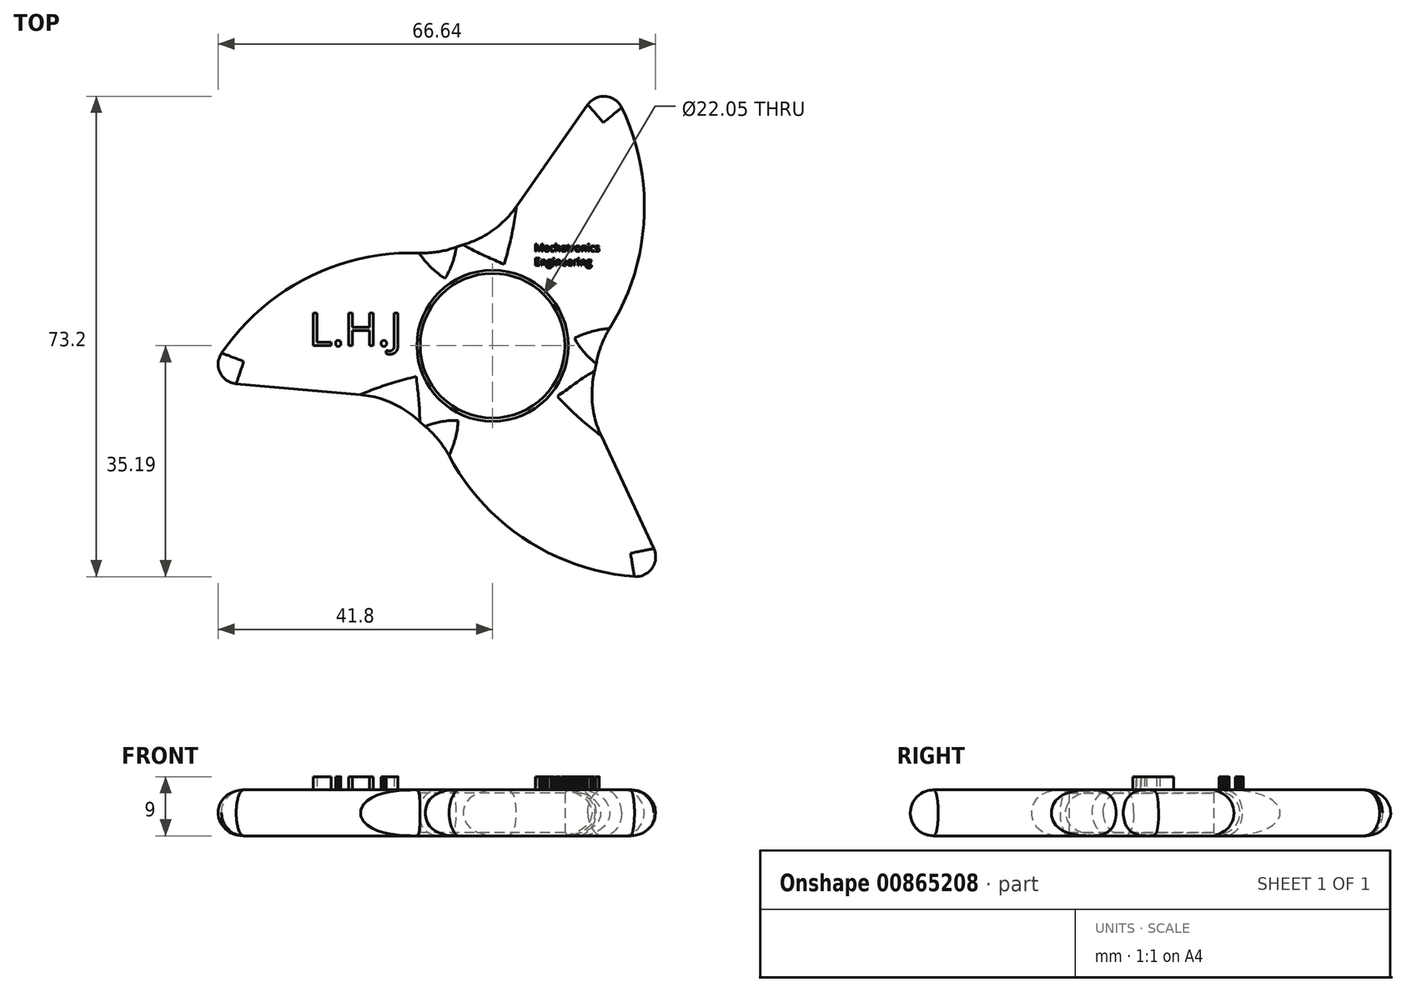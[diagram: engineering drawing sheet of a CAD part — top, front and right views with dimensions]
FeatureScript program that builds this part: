
annotation { "Feature Type Name" : "Feature", "Feature Type Description" : "" }
export const myFeature = defineFeature(function(context is Context, id is Id, definition is map)
    precondition{}
    {
        {
            var Q0;
            Q0=qCreatedBy(makeId("Top.planeOp"),FACE);
            var sketch = newSketch(context, id + "F0", { "sketchPlane" : qUnion([Q0])});
            skCircle(sketch, "E0", {"center": v(0, 0) * mm, "radius": 11.03 * mm});
            skCircle(sketch, "E1", {"center": v(0, 0) * mm, "radius": 16.03 * mm});
            skLineSegment(sketch, "E2", {"start": v(0, 16.02) * mm, "end": v(14.5, 36.73) * mm});
            skArc(sketch, "E3", {"start": v(16.03, 0) * mm, "mid": v(22.95, 17.64) * mm, "end": v(19.66, 36.31) * mm});
            skPoint(sketch, "E4.visualSharp", {"position": v(17.2, 40.6) * mm});
            skArc(sketch, "E4.filletArc", {"start": v(19.66, 36.31) * mm, "mid": v(17.2, 38) * mm, "end": v(14.5, 36.73) * mm});
            skSolve(sketch);
        }
        {
            var Q0;
            Q0=qSketchRegion(id+"F0",true);
            extrude(context, id + "F1", {"entities" : qUnion([Q0]), "depth" : 7 * mm, "offsetDistance" : 25 * mm});
        }
        {
            var Q0;
            Q0=qCreatedBy(makeId("Right.planeOp"),FACE);
            var sketch = newSketch(context, id + "F2", { "sketchPlane" : qUnion([Q0])});
            skLineSegment(sketch, "E5", {"start": v(0, 0) * mm, "end": v(0, -17.5) * mm});
            skSolve(sketch);
        }
        {
            var Q0;
            Q0=makeQuery(id+"F1.opExtrude","CAP_EDGE",EDGE,{"disambiguationData":[OSD([sQuery(id+"F0.wireOp",EDGE,"E3")])],"isStart":false});
            var Q1;
            Q1=makeQuery(id+"F1.opExtrude","CAP_EDGE",EDGE,{"disambiguationData":[OSD([sQuery(id+"F0.wireOp",EDGE,"E3")])],"isStart":true});
            var Q2;
            Q2=makeQuery(id+"F1.opExtrude","CAP_EDGE",EDGE,{"disambiguationData":[OSD([sQuery(id+"F0.wireOp",EDGE,"E1")])],"isStart":true});
            var Q3;
            Q3=makeQuery(id+"F1.opExtrude","CAP_EDGE",EDGE,{"disambiguationData":[OSD([sQuery(id+"F0.wireOp",EDGE,"E1")])],"isStart":false});
            fillet(context, id + "F3", {"entities" : qUnion([Q0, Q1, Q2, Q3]), "radius" : 3.5 * mm, "tangentPropagation" : true, "allowEdgeOverflow" : false});
        }
        {
            var Q0;
            Q0=makeQuery(id+"F1.opExtrude","SWEPT_BODY",BODY,{"disambiguationData":[OSD([sQuery(id+"F0.wireOp",EDGE,"E0"),sQuery(id+"F0.wireOp",EDGE,"E1"),sQuery(id+"F0.wireOp",EDGE,"E2"),sQuery(id+"F0.wireOp",EDGE,"E3"),sQuery(id+"F0.wireOp",EDGE,"E4.filletArc")])]});
            var Q1;
            Q1=sQuery(id+"F2.wireOp",EDGE,"E5");
            circularPattern(context, id + "F4", {"entities" : qUnion([Q0]), "axis" : qUnion([Q1]), "angle" : 360 * degree, "instanceCount" : 3, "equalSpace" : true});
        }
        {
            var Q0;
            Q0=makeQuery(id+"F1.opExtrude","SWEPT_BODY",BODY,{"disambiguationData":[OSD([sQuery(id+"F0.wireOp",EDGE,"E0"),sQuery(id+"F0.wireOp",EDGE,"E1"),sQuery(id+"F0.wireOp",EDGE,"E2"),sQuery(id+"F0.wireOp",EDGE,"E3"),sQuery(id+"F0.wireOp",EDGE,"E4.filletArc")])]});
            var Q1;
            Q1=makeQuery(id+"F4.opPattern","COPY",BODY,{"derivedFrom":makeQuery(id+"F1.opExtrude","SWEPT_BODY",BODY,{"disambiguationData":[OSD([sQuery(id+"F0.wireOp",EDGE,"E0"),sQuery(id+"F0.wireOp",EDGE,"E1"),sQuery(id+"F0.wireOp",EDGE,"E2"),sQuery(id+"F0.wireOp",EDGE,"E3"),sQuery(id+"F0.wireOp",EDGE,"E4.filletArc")])]}),"instanceName":"1"});
            var Q2;
            Q2=makeQuery(id+"F4.opPattern","COPY",BODY,{"derivedFrom":makeQuery(id+"F1.opExtrude","SWEPT_BODY",BODY,{"disambiguationData":[OSD([sQuery(id+"F0.wireOp",EDGE,"E0"),sQuery(id+"F0.wireOp",EDGE,"E1"),sQuery(id+"F0.wireOp",EDGE,"E2"),sQuery(id+"F0.wireOp",EDGE,"E3"),sQuery(id+"F0.wireOp",EDGE,"E4.filletArc")])]}),"instanceName":"2"});
            booleanBodies(context, id + "F5", {"operationType" : BooleanOperationType.UNION, "tools" : qUnion([Q0, Q1, Q2])});
        }
        {
            var Q0;
            {var subQ0=sQuery(id+"F0.wireOp",EDGE,"E2");var subQ1=sQuery(id+"F0.wireOp",EDGE,"E1");Q0=makeQuery(id+"F5.opBoolean","MERGE",EDGE,{"derivedFrom":[makeQuery(id+"F3.opFillet","BLEND_EDGE",EDGE,{"blendedFrom":[makeQuery(id+"F1.opExtrude","CAP_EDGE",EDGE,{"disambiguationData":[OSD([subQ1])],"isStart":true}),makeQuery(id+"F1.opExtrude","CAP_EDGE",EDGE,{"disambiguationData":[OSD([subQ0])],"isStart":true})],"blendedInto":[]}),makeQuery(id+"F3.opFillet","BLEND_EDGE",EDGE,{"blendedFrom":[makeQuery(id+"F1.opExtrude","CAP_EDGE",EDGE,{"disambiguationData":[OSD([subQ1])],"isStart":false}),makeQuery(id+"F1.opExtrude","CAP_EDGE",EDGE,{"disambiguationData":[OSD([subQ0])],"isStart":false})],"blendedInto":[]})]});}
            var Q1;
            {var subQ0=sQuery(id+"F0.wireOp",EDGE,"E3");var subQ1=sQuery(id+"F0.wireOp",EDGE,"E1");Q1=makeQuery(id+"F5.opBoolean","MERGE",EDGE,{"derivedFrom":[makeQuery(id+"F4.opPattern","COPY",EDGE,{"derivedFrom":makeQuery(id+"F3.opFillet","BLEND_EDGE",EDGE,{"blendedFrom":[makeQuery(id+"F1.opExtrude","CAP_EDGE",EDGE,{"disambiguationData":[OSD([subQ1])],"isStart":true}),makeQuery(id+"F1.opExtrude","CAP_EDGE",EDGE,{"disambiguationData":[OSD([subQ0])],"isStart":true})],"blendedInto":[]}),"instanceName":"2"}),makeQuery(id+"F4.opPattern","COPY",EDGE,{"derivedFrom":makeQuery(id+"F3.opFillet","BLEND_EDGE",EDGE,{"blendedFrom":[makeQuery(id+"F1.opExtrude","CAP_EDGE",EDGE,{"disambiguationData":[OSD([subQ1])],"isStart":false}),makeQuery(id+"F1.opExtrude","CAP_EDGE",EDGE,{"disambiguationData":[OSD([subQ0])],"isStart":false})],"blendedInto":[]}),"instanceName":"2"})]});}
            var Q2;
            {var subQ0=sQuery(id+"F0.wireOp",EDGE,"E3");var subQ1=sQuery(id+"F0.wireOp",EDGE,"E1");Q2=makeQuery(id+"F5.opBoolean","MERGE",EDGE,{"derivedFrom":[makeQuery(id+"F3.opFillet","BLEND_EDGE",EDGE,{"blendedFrom":[makeQuery(id+"F1.opExtrude","CAP_EDGE",EDGE,{"disambiguationData":[OSD([subQ1])],"isStart":true}),makeQuery(id+"F1.opExtrude","CAP_EDGE",EDGE,{"disambiguationData":[OSD([subQ0])],"isStart":true})],"blendedInto":[]}),makeQuery(id+"F3.opFillet","BLEND_EDGE",EDGE,{"blendedFrom":[makeQuery(id+"F1.opExtrude","CAP_EDGE",EDGE,{"disambiguationData":[OSD([subQ1])],"isStart":false}),makeQuery(id+"F1.opExtrude","CAP_EDGE",EDGE,{"disambiguationData":[OSD([subQ0])],"isStart":false})],"blendedInto":[]})]});}
            var Q3;
            {var subQ0=sQuery(id+"F0.wireOp",EDGE,"E2");var subQ1=sQuery(id+"F0.wireOp",EDGE,"E1");Q3=makeQuery(id+"F5.opBoolean","MERGE",EDGE,{"derivedFrom":[makeQuery(id+"F4.opPattern","COPY",EDGE,{"derivedFrom":makeQuery(id+"F3.opFillet","BLEND_EDGE",EDGE,{"blendedFrom":[makeQuery(id+"F1.opExtrude","CAP_EDGE",EDGE,{"disambiguationData":[OSD([subQ1])],"isStart":true}),makeQuery(id+"F1.opExtrude","CAP_EDGE",EDGE,{"disambiguationData":[OSD([subQ0])],"isStart":true})],"blendedInto":[]}),"instanceName":"1"}),makeQuery(id+"F4.opPattern","COPY",EDGE,{"derivedFrom":makeQuery(id+"F3.opFillet","BLEND_EDGE",EDGE,{"blendedFrom":[makeQuery(id+"F1.opExtrude","CAP_EDGE",EDGE,{"disambiguationData":[OSD([subQ1])],"isStart":false}),makeQuery(id+"F1.opExtrude","CAP_EDGE",EDGE,{"disambiguationData":[OSD([subQ0])],"isStart":false})],"blendedInto":[]}),"instanceName":"1"})]});}
            var Q4;
            {var subQ0=sQuery(id+"F0.wireOp",EDGE,"E3");var subQ1=sQuery(id+"F0.wireOp",EDGE,"E1");Q4=makeQuery(id+"F5.opBoolean","MERGE",EDGE,{"derivedFrom":[makeQuery(id+"F4.opPattern","COPY",EDGE,{"derivedFrom":makeQuery(id+"F3.opFillet","BLEND_EDGE",EDGE,{"blendedFrom":[makeQuery(id+"F1.opExtrude","CAP_EDGE",EDGE,{"disambiguationData":[OSD([subQ1])],"isStart":true}),makeQuery(id+"F1.opExtrude","CAP_EDGE",EDGE,{"disambiguationData":[OSD([subQ0])],"isStart":true})],"blendedInto":[]}),"instanceName":"1"}),makeQuery(id+"F4.opPattern","COPY",EDGE,{"derivedFrom":makeQuery(id+"F3.opFillet","BLEND_EDGE",EDGE,{"blendedFrom":[makeQuery(id+"F1.opExtrude","CAP_EDGE",EDGE,{"disambiguationData":[OSD([subQ1])],"isStart":false}),makeQuery(id+"F1.opExtrude","CAP_EDGE",EDGE,{"disambiguationData":[OSD([subQ0])],"isStart":false})],"blendedInto":[]}),"instanceName":"1"})]});}
            var Q5;
            {var subQ0=sQuery(id+"F0.wireOp",EDGE,"E2");var subQ1=sQuery(id+"F0.wireOp",EDGE,"E1");Q5=makeQuery(id+"F5.opBoolean","MERGE",EDGE,{"derivedFrom":[makeQuery(id+"F4.opPattern","COPY",EDGE,{"derivedFrom":makeQuery(id+"F3.opFillet","BLEND_EDGE",EDGE,{"blendedFrom":[makeQuery(id+"F1.opExtrude","CAP_EDGE",EDGE,{"disambiguationData":[OSD([subQ1])],"isStart":true}),makeQuery(id+"F1.opExtrude","CAP_EDGE",EDGE,{"disambiguationData":[OSD([subQ0])],"isStart":true})],"blendedInto":[]}),"instanceName":"2"}),makeQuery(id+"F4.opPattern","COPY",EDGE,{"derivedFrom":makeQuery(id+"F3.opFillet","BLEND_EDGE",EDGE,{"blendedFrom":[makeQuery(id+"F1.opExtrude","CAP_EDGE",EDGE,{"disambiguationData":[OSD([subQ1])],"isStart":false}),makeQuery(id+"F1.opExtrude","CAP_EDGE",EDGE,{"disambiguationData":[OSD([subQ0])],"isStart":false})],"blendedInto":[]}),"instanceName":"2"})]});}
            fillet(context, id + "F6", {"entities" : qUnion([Q0, Q1, Q2, Q3, Q4, Q5]), "radius" : 15 * mm, "tangentPropagation" : true, "allowEdgeOverflow" : false});
        }
        {
            var Q0;
            Q0=makeQuery(id+"F1.opExtrude","CAP_EDGE",EDGE,{"disambiguationData":[OSD([sQuery(id+"F0.wireOp",EDGE,"E0")])],"isStart":false});
            var Q1;
            Q1=makeQuery(id+"F1.opExtrude","CAP_EDGE",EDGE,{"disambiguationData":[OSD([sQuery(id+"F0.wireOp",EDGE,"E0")])],"isStart":true});
            chamfer(context, id + "F7", {"entities" : qUnion([Q0, Q1]), "width" : .5 * mm, "tangentPropagation" : true});
        }
        {
            var Q0;
            {var subQ0=makeQuery(id+"F1.opExtrude","CAP_FACE",FACE,{"disambiguationData":[OSD([sQuery(id+"F0.wireOp",EDGE,"E0"),sQuery(id+"F0.wireOp",EDGE,"E1"),sQuery(id+"F0.wireOp",EDGE,"E2"),sQuery(id+"F0.wireOp",EDGE,"E3"),sQuery(id+"F0.wireOp",EDGE,"E4.filletArc")])],"isStart":false});Q0=makeQuery(id+"F5.opBoolean","MERGE",FACE,{"derivedFrom":[subQ0,makeQuery(id+"F4.opPattern","COPY",FACE,{"derivedFrom":subQ0,"instanceName":"1"}),makeQuery(id+"F4.opPattern","COPY",FACE,{"derivedFrom":subQ0,"instanceName":"2"})]});}
            var sketch = newSketch(context, id + "F8", { "sketchPlane" : qUnion([Q0])});
            skText(sketch, "E6", { "text": "L.H.J", "fontName": "OpenSans-Regular.ttf"});
            const initialGuessF8  = {"E6": [-0.02803, 0, 1, 0, 0.00499]};
            skSetInitialGuess(sketch, initialGuessF8);
            skSolve(sketch);
        }
        {
            var Q0;
            Q0=makeQuery(id+"F8.imprint","IMPRINT",FACE,{"disambiguationData":[TD([[makeQuery(id+"F8.imprint","IMPRINT",EDGE,{"derivedFrom":sQuery(id+"F8.wireOp",EDGE,"E6.sketch_text.stroke-0")}),1.0]])]});
            var sketch = newSketch(context, id + "F9", { "sketchPlane" : qUnion([Q0])});
            skText(sketch, "E7", { "text": "Mechatronics\nEngineering", "fontName": "OpenSans-Regular.ttf"});
            const initialGuessF9  = {"E7": [0.00637, 0.01437, 1, 0, 0.00114]};
            skSetInitialGuess(sketch, initialGuessF9);
            skSolve(sketch);
        }
        {
            var Q0;
            Q0 = qSketchRegion(id + "F8", true);
            extrude(context, id + "F10", {"entities" : qUnion([Q0]), "operationType" : NewBodyOperationType.ADD, "depth" : 2 * mm, "offsetDistance" : 25 * mm});
        }
        {
            var Q0;
            Q0 = qSketchRegion(id + "F9", true);
            extrude(context, id + "F11", {"entities" : qUnion([Q0]), "operationType" : NewBodyOperationType.ADD, "depth" : 2 * mm, "offsetDistance" : 25 * mm});
        }
    });
